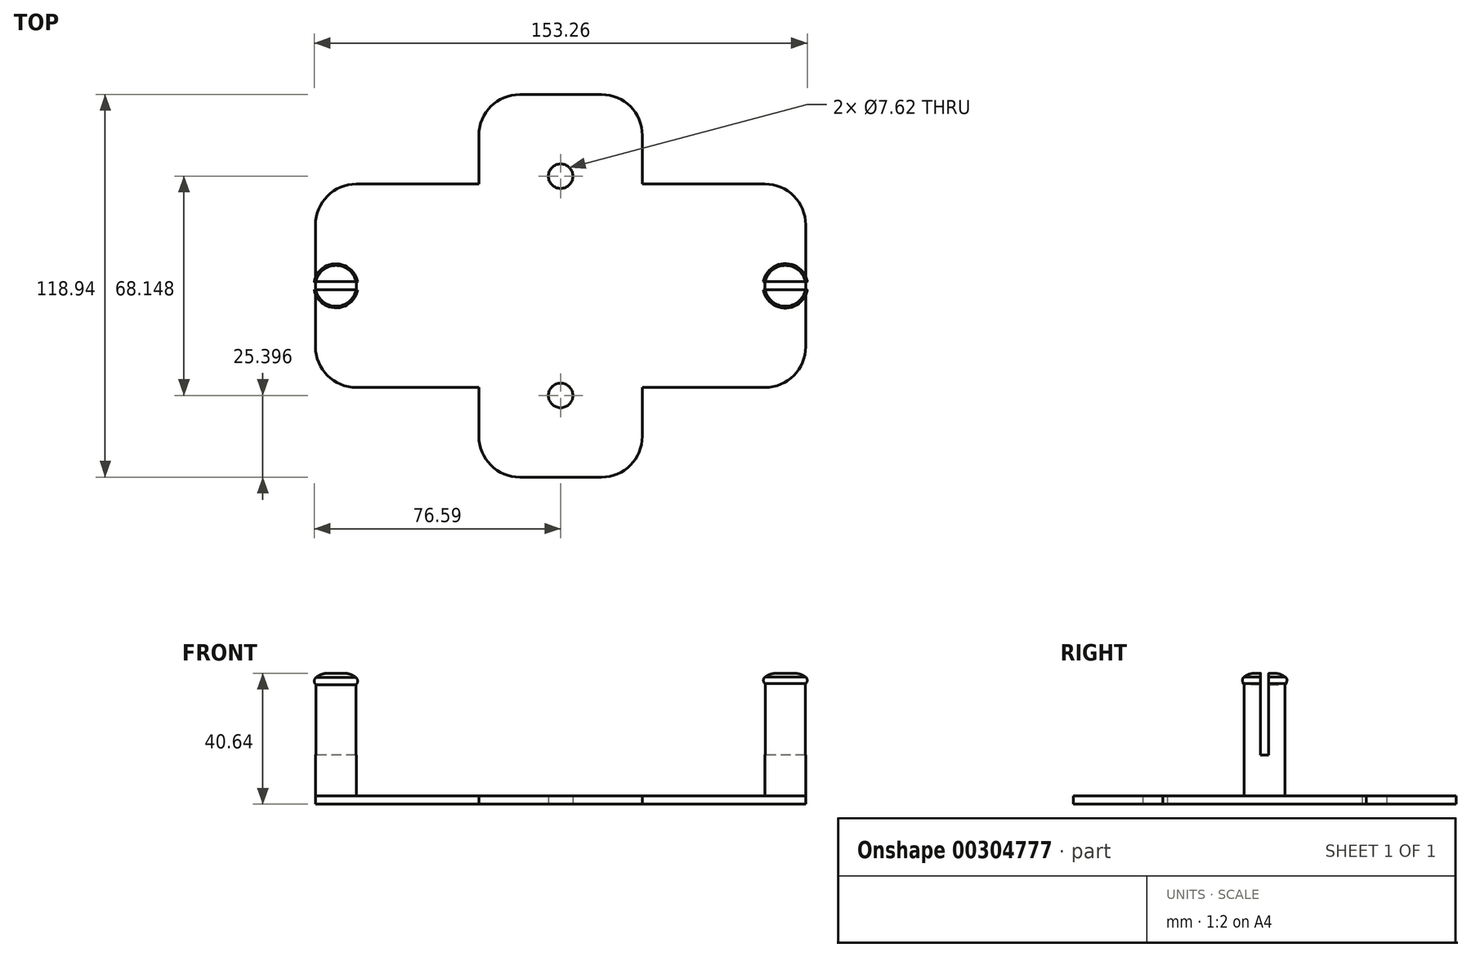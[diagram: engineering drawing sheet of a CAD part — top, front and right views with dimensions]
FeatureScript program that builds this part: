
annotation { "Feature Type Name" : "Feature", "Feature Type Description" : "" }
export const myFeature = defineFeature(function(context is Context, id is Id, definition is map)
    precondition{}
    {
        {
            var Q0;
            Q0=qCreatedBy(makeId("Top.planeOp"),FACE);
            var sketch = newSketch(context, id + "F0", { "sketchPlane" : qUnion([Q0])});
            skPoint(sketch, "E0.rect.middle", {"position": v(0, 0) * mm});
            skCircle(sketch, "E1", {"center": v(0, 34.07) * mm, "radius": 3.81 * mm});
            skCircle(sketch, "E2", {"center": v(0, -34.07) * mm, "radius": 3.81 * mm});
            skLineSegment(sketch, "E3.top", {"start": v(76.2, 31.61) * mm, "end": v(25.4, 31.61) * mm});
            skLineSegment(sketch, "E3.right", {"start": v(25.4, 59.47) * mm, "end": v(25.4, 31.61) * mm});
            skLineSegment(sketch, "E4.0.MirrorCS", {"start": v(-25.4, 59.47) * mm, "end": v(-25.4, 31.61) * mm});
            skLineSegment(sketch, "E5.0.MirrorCS", {"start": v(-76.2, 31.61) * mm, "end": v(-25.4, 31.61) * mm});
            skLineSegment(sketch, "E6.0.MirrorCS", {"start": v(76.2, -31.61) * mm, "end": v(25.4, -31.61) * mm});
            skLineSegment(sketch, "E7.0.MirrorCS", {"start": v(25.4, -59.47) * mm, "end": v(25.4, -31.61) * mm});
            skLineSegment(sketch, "E8.0.MirrorCS", {"start": v(-76.2, -31.61) * mm, "end": v(-25.4, -31.61) * mm});
            skLineSegment(sketch, "E9.0.MirrorCS", {"start": v(-25.4, -59.47) * mm, "end": v(-25.4, -31.61) * mm});
            skLineSegment(sketch, "E10", {"start": v(-25.4, 59.47) * mm, "end": v(25.4, 59.47) * mm});
            skLineSegment(sketch, "E11", {"start": v(76.2, 31.61) * mm, "end": v(76.2, -31.61) * mm});
            skLineSegment(sketch, "E12", {"start": v(25.4, -59.47) * mm, "end": v(-25.4, -59.47) * mm});
            skLineSegment(sketch, "E13", {"start": v(-76.2, -31.61) * mm, "end": v(-76.2, 31.61) * mm});
            skSolve(sketch);
        }
        {
            var Q0;
            Q0=makeQuery(id+"F0.imprint","IMPRINT",FACE,{"disambiguationData":[TD([[makeQuery(id+"F0.imprint","IMPRINT",EDGE,{"derivedFrom":sQuery(id+"F0.wireOp",EDGE,"E1")}),-1.0]])]});
            extrude(context, id + "F1", {"entities" : qUnion([Q0]), "depth" : 2.54 * mm});
        }
        {
            var Q0;
            Q0=makeQuery(id+"F1.opExtrude","CAP_FACE",FACE,{"disambiguationData":[OSD([sQuery(id+"F0.wireOp",EDGE,"E1"),sQuery(id+"F0.wireOp",EDGE,"E2"),sQuery(id+"F0.wireOp",EDGE,"E3.top"),sQuery(id+"F0.wireOp",EDGE,"E3.right"),sQuery(id+"F0.wireOp",EDGE,"E4.0.MirrorCS"),sQuery(id+"F0.wireOp",EDGE,"E5.0.MirrorCS"),sQuery(id+"F0.wireOp",EDGE,"E6.0.MirrorCS"),sQuery(id+"F0.wireOp",EDGE,"E7.0.MirrorCS"),sQuery(id+"F0.wireOp",EDGE,"E8.0.MirrorCS"),sQuery(id+"F0.wireOp",EDGE,"E9.0.MirrorCS"),sQuery(id+"F0.wireOp",EDGE,"E10"),sQuery(id+"F0.wireOp",EDGE,"E11"),sQuery(id+"F0.wireOp",EDGE,"E12"),sQuery(id+"F0.wireOp",EDGE,"E13")])],"isStart":false});
            var sketch = newSketch(context, id + "F2", { "sketchPlane" : qUnion([Q0])});
            skCircle(sketch, "E14", {"center": v(69.85, 0) * mm, "radius": 6.35 * mm});
            skCircle(sketch, "E15", {"center": v(-69.85, 0) * mm, "radius": 6.35 * mm});
            skSolve(sketch);
        }
        {
            var Q0;
            Q0=qSketchRegion(id+"F2",true);
            extrude(context, id + "F3", {"entities" : qUnion([Q0]), "operationType" : NewBodyOperationType.ADD, "depth" : 38.1 * mm});
        }
        {
            var Q0;
            Q0=qCreatedBy(makeId("Front.planeOp"),FACE);
            var sketch = newSketch(context, id + "F4", { "sketchPlane" : qUnion([Q0])});
            skArc(sketch, "E16", {"start": v(63.5, 39.54) * mm, "mid": v(62.91, 38.48) * mm, "end": v(63.5, 37.41) * mm});
            skLineSegment(sketch, "E17", {"start": v(63.5, 39.54) * mm, "end": v(63.5, 37.41) * mm});
            skSolve(sketch);
        }
        {
            var Q0;
            Q0=makeQuery(id+"F4.imprint","IMPRINT",FACE,{"disambiguationData":[TD([[makeQuery(id+"F4.imprint","IMPRINT",EDGE,{"derivedFrom":sQuery(id+"F4.wireOp",EDGE,"E16")}),1.0]])]});
            var Q1;
            Q1=makeQuery(id+"F3.opExtrude","CAP_EDGE",EDGE,{"disambiguationData":[OSD([sQuery(id+"F2.wireOp",EDGE,"E14")])],"isStart":false});
            sweep(context, id + "F5", {"operationType" : NewBodyOperationType.ADD, "profiles" : qUnion([Q0]), "path" : qUnion([Q1])});
        }
        {
            var Q0;
            Q0=makeQuery(id+"F3.opExtrude","CAP_EDGE",EDGE,{"disambiguationData":[OSD([sQuery(id+"F2.wireOp",EDGE,"E14")])],"isStart":false});
            fillet(context, id + "F6", {"entities" : qUnion([Q0]), "radius" : 5.08 * mm, "tangentPropagation" : true, "allowEdgeOverflow" : false});
        }
        {
            var Q0;
            Q0=qCreatedBy(makeId("Front.planeOp"),FACE);
            var sketch = newSketch(context, id + "F7", { "sketchPlane" : qUnion([Q0])});
            skArc(sketch, "E18", {"start": v(-63.57, 37.03) * mm, "mid": v(-63, 38.2) * mm, "end": v(-63.58, 39.37) * mm});
            skLineSegment(sketch, "E19", {"start": v(-63.58, 39.37) * mm, "end": v(-63.57, 37.03) * mm});
            skSolve(sketch);
        }
        {
            var Q0;
            Q0=makeQuery(id+"F7.imprint","IMPRINT",FACE,{"disambiguationData":[TD([[makeQuery(id+"F7.imprint","IMPRINT",EDGE,{"derivedFrom":sQuery(id+"F7.wireOp",EDGE,"E18")}),1.0]])]});
            var Q1;
            Q1=makeQuery(id+"F3.opExtrude","CAP_EDGE",EDGE,{"disambiguationData":[OSD([sQuery(id+"F2.wireOp",EDGE,"E15")])],"isStart":false});
            sweep(context, id + "F8", {"operationType" : NewBodyOperationType.ADD, "profiles" : qUnion([Q0]), "path" : qUnion([Q1])});
        }
        {
            var Q0;
            Q0=makeQuery(id+"F3.opExtrude","CAP_EDGE",EDGE,{"disambiguationData":[OSD([sQuery(id+"F2.wireOp",EDGE,"E15")])],"isStart":false});
            fillet(context, id + "F9", {"entities" : qUnion([Q0]), "radius" : 5.08 * mm, "tangentPropagation" : true, "allowEdgeOverflow" : false});
        }
        {
            var Q0;
            Q0=makeQuery(id+"F1.opExtrude","SWEPT_EDGE",EDGE,{"disambiguationData":[OSD([sQuery(id+"F0.wireOp",EDGE,"E6.0.MirrorCS"),sQuery(id+"F0.wireOp",EDGE,"E11")])]});
            var Q1;
            Q1=makeQuery(id+"F1.opExtrude","SWEPT_EDGE",EDGE,{"disambiguationData":[OSD([sQuery(id+"F0.wireOp",EDGE,"E3.top"),sQuery(id+"F0.wireOp",EDGE,"E11")])]});
            var Q2;
            Q2=makeQuery(id+"F1.opExtrude","SWEPT_EDGE",EDGE,{"disambiguationData":[OSD([sQuery(id+"F0.wireOp",EDGE,"E5.0.MirrorCS"),sQuery(id+"F0.wireOp",EDGE,"E13")])]});
            var Q3;
            Q3=makeQuery(id+"F1.opExtrude","SWEPT_EDGE",EDGE,{"disambiguationData":[OSD([sQuery(id+"F0.wireOp",EDGE,"E8.0.MirrorCS"),sQuery(id+"F0.wireOp",EDGE,"E13")])]});
            var Q4;
            Q4=makeQuery(id+"F1.opExtrude","SWEPT_EDGE",EDGE,{"disambiguationData":[OSD([sQuery(id+"F0.wireOp",EDGE,"E9.0.MirrorCS"),sQuery(id+"F0.wireOp",EDGE,"E12")])]});
            var Q5;
            Q5=makeQuery(id+"F1.opExtrude","SWEPT_EDGE",EDGE,{"disambiguationData":[OSD([sQuery(id+"F0.wireOp",EDGE,"E7.0.MirrorCS"),sQuery(id+"F0.wireOp",EDGE,"E12")])]});
            var Q6;
            Q6=makeQuery(id+"F1.opExtrude","SWEPT_EDGE",EDGE,{"disambiguationData":[OSD([sQuery(id+"F0.wireOp",EDGE,"E3.right"),sQuery(id+"F0.wireOp",EDGE,"E10")])]});
            var Q7;
            Q7=makeQuery(id+"F1.opExtrude","SWEPT_EDGE",EDGE,{"disambiguationData":[OSD([sQuery(id+"F0.wireOp",EDGE,"E4.0.MirrorCS"),sQuery(id+"F0.wireOp",EDGE,"E10")])]});
            fillet(context, id + "F10", {"entities" : qUnion([Q0, Q1, Q2, Q3, Q4, Q5, Q6, Q7]), "radius" : 12.7 * mm, "tangentPropagation" : true, "allowEdgeOverflow" : false});
        }
        {
            var Q0;
            Q0=makeQuery(id+"F3.opExtrude","CAP_FACE",FACE,{"disambiguationData":[OSD([sQuery(id+"F2.wireOp",EDGE,"E14")])],"isStart":false});
            var sketch = newSketch(context, id + "F11", { "sketchPlane" : qUnion([Q0])});
            skLineSegment(sketch, "E20.rect.bottom", {"start": v(77.48, 1.27) * mm, "end": v(62.22, 1.27) * mm});
            skLineSegment(sketch, "E20.rect.top", {"start": v(77.48, -1.27) * mm, "end": v(62.22, -1.27) * mm});
            skLineSegment(sketch, "E20.rect.left", {"start": v(77.48, 1.27) * mm, "end": v(77.48, -1.27) * mm});
            skLineSegment(sketch, "E20.rect.right", {"start": v(62.22, 1.27) * mm, "end": v(62.22, -1.27) * mm});
            skPoint(sketch, "E20.rect.middle", {"position": v(69.85, 0) * mm});
            skSolve(sketch);
        }
        {
            var Q0;
            Q0=qSketchRegion(id+"F11",true);
            extrude(context, id + "F12", {"entities" : qUnion([Q0]), "operationType" : NewBodyOperationType.REMOVE, "oppositeDirection" : true, "depth" : 25.4 * mm});
        }
        {
            var Q0;
            Q0=makeQuery(id+"F3.opExtrude","CAP_FACE",FACE,{"disambiguationData":[OSD([sQuery(id+"F2.wireOp",EDGE,"E15")])],"isStart":false});
            var sketch = newSketch(context, id + "F13", { "sketchPlane" : qUnion([Q0])});
            skLineSegment(sketch, "E21.rect.bottom", {"start": v(-62.58, 1.27) * mm, "end": v(-77.12, 1.27) * mm});
            skLineSegment(sketch, "E21.rect.top", {"start": v(-62.58, -1.27) * mm, "end": v(-77.12, -1.27) * mm});
            skLineSegment(sketch, "E21.rect.left", {"start": v(-62.58, 1.27) * mm, "end": v(-62.58, -1.27) * mm});
            skLineSegment(sketch, "E21.rect.right", {"start": v(-77.12, 1.27) * mm, "end": v(-77.12, -1.27) * mm});
            skPoint(sketch, "E21.rect.middle", {"position": v(-69.85, 0) * mm});
            skSolve(sketch);
        }
        {
            var Q0;
            Q0=qSketchRegion(id+"F13",true);
            extrude(context, id + "F14", {"entities" : qUnion([Q0]), "operationType" : NewBodyOperationType.REMOVE, "oppositeDirection" : true, "depth" : 25.4 * mm});
        }
    });
